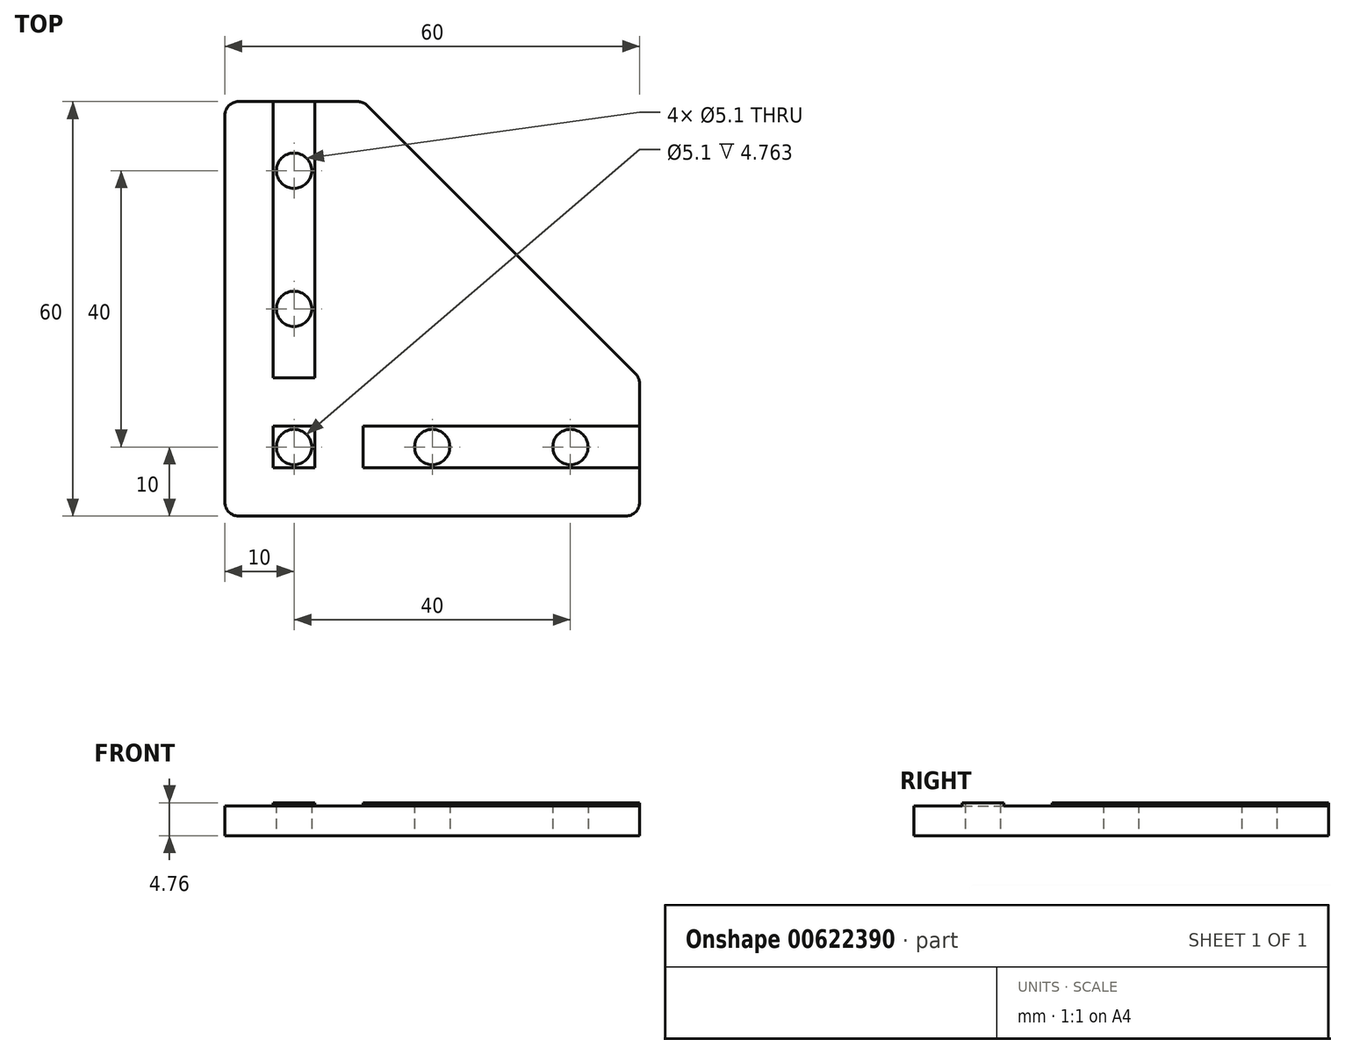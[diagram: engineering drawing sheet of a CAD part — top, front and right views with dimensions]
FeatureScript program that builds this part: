
annotation { "Feature Type Name" : "Feature", "Feature Type Description" : "" }
export const myFeature = defineFeature(function(context is Context, id is Id, definition is map)
    precondition{}
    {
        {
            assignVariable(context, id + "F0", {"name" : "TotalThick", "anyValue" : 4.76});
        }
        {
            assignVariable(context, id + "F1", {"name" : "Recess", "anyValue" : 0.5});
        }
        {
            var Q0;
            Q0=qCreatedBy(makeId("Top.planeOp"),FACE);
            var sketch = newSketch(context, id + "F2", { "sketchPlane" : qUnion([Q0])});
            skLineSegment(sketch, "E0", {"start": v(-10, 50) * mm, "end": v(-10, -10) * mm});
            skLineSegment(sketch, "E1", {"start": v(-10, -10) * mm, "end": v(50, -10) * mm});
            skLineSegment(sketch, "E2", {"start": v(50, -10) * mm, "end": v(50, 10) * mm});
            skLineSegment(sketch, "E3", {"start": v(50, 10) * mm, "end": v(10, 50) * mm});
            skLineSegment(sketch, "E4", {"start": v(10, 50) * mm, "end": v(-10, 50) * mm});
            skCircle(sketch, "E5", {"center": v(0, 0) * mm, "radius": 2.55 * mm});
            skCircle(sketch, "E6", {"center": v(0, 20) * mm, "radius": 2.55 * mm});
            skCircle(sketch, "E7", {"center": v(0, 40) * mm, "radius": 2.55 * mm});
            skCircle(sketch, "E8", {"center": v(20, 0) * mm, "radius": 2.55 * mm});
            skCircle(sketch, "E9", {"center": v(40, 0) * mm, "radius": 2.55 * mm});
            skLineSegment(sketch, "E10", {"start": v(-3.02, 50) * mm, "end": v(-3.03, -10) * mm});
            skLineSegment(sketch, "E11.MirrorCS", {"start": v(3.03, 50) * mm, "end": v(3.02, -10) * mm});
            skLineSegment(sketch, "E12", {"start": v(-10, 3.03) * mm, "end": v(50, 3.02) * mm});
            skLineSegment(sketch, "E13.MirrorCS", {"start": v(-10, -3.03) * mm, "end": v(50, -3.02) * mm});
            skLineSegment(sketch, "E14", {"start": v(10, 50) * mm, "end": v(10, -10) * mm});
            skLineSegment(sketch, "E15", {"start": v(50, 10) * mm, "end": v(-10, 10) * mm});
            skSolve(sketch);
        }
        {
            var Q0;
            Q0=qSketchRegion(id+"F2",true);
            var Q1;
            {var subQ0=sQuery(id+"F2.wireOp",EDGE,"E15");var subQ1=sQuery(id+"F2.wireOp",EDGE,"E11.MirrorCS");var subQ2=makeQuery(id+"F2.imprint","INTERSECT",VERTEX,{"derivedFrom":[subQ1,subQ0]});Q1=makeQuery(id+"F2.imprint","IMPRINT",FACE,{"disambiguationData":[TD([[makeQuery(id+"F2.imprint","IMPRINT",EDGE,{"disambiguationData":[TD([[subQ2,-1.0]])],"derivedFrom":subQ1}),1.0]])]});}
            var Q2;
            {var subQ0=sQuery(id+"F2.wireOp",EDGE,"E12");var subQ1=sQuery(id+"F2.wireOp",EDGE,"E11.MirrorCS");var subQ2=makeQuery(id+"F2.imprint","INTERSECT",VERTEX,{"derivedFrom":[subQ1,subQ0]});Q2=makeQuery(id+"F2.imprint","IMPRINT",FACE,{"disambiguationData":[TD([[makeQuery(id+"F2.imprint","IMPRINT",EDGE,{"disambiguationData":[TD([[subQ2,-1.0]])],"derivedFrom":subQ1}),1.0]])]});}
            var Q3;
            Q3=makeQuery(id+"F2.imprint","IMPRINT",FACE,{"disambiguationData":[TD([[makeQuery(id+"F2.imprint","IMPRINT",EDGE,{"derivedFrom":sQuery(id+"F2.wireOp",EDGE,"E5")}),-1.0]])]});
            var Q4;
            {var subQ0=sQuery(id+"F2.wireOp",EDGE,"E15");var subQ1=sQuery(id+"F2.wireOp",EDGE,"E10");var subQ2=makeQuery(id+"F2.imprint","INTERSECT",VERTEX,{"derivedFrom":[subQ1,subQ0]});Q4=makeQuery(id+"F2.imprint","IMPRINT",FACE,{"disambiguationData":[TD([[makeQuery(id+"F2.imprint","IMPRINT",EDGE,{"disambiguationData":[TD([[subQ2,-1.0]])],"derivedFrom":subQ1}),1.0]])]});}
            extrude(context, id + "F3", {"entities" : qUnion([Q0, Q1, Q2, Q3, Q4]), "depth" : (getVariable(context, 'TotalThick') - getVariable(context, 'Recess')) * mm, "offsetDistance" : 25 * mm});
        }
        {
            var Q0;
            Q0=makeQuery(id+"F2.imprint","IMPRINT",FACE,{"disambiguationData":[TD([[makeQuery(id+"F2.imprint","IMPRINT",EDGE,{"derivedFrom":sQuery(id+"F2.wireOp",EDGE,"E5")}),-1.0]])]});
            var Q1;
            Q1=makeQuery(id+"F2.imprint","IMPRINT",FACE,{"disambiguationData":[TD([[makeQuery(id+"F2.imprint","IMPRINT",EDGE,{"derivedFrom":sQuery(id+"F2.wireOp",EDGE,"E8")}),-1.0]])]});
            var Q2;
            Q2=makeQuery(id+"F2.imprint","IMPRINT",FACE,{"disambiguationData":[TD([[makeQuery(id+"F2.imprint","IMPRINT",EDGE,{"derivedFrom":sQuery(id+"F2.wireOp",EDGE,"E6")}),-1.0]])]});
            extrude(context, id + "F4", {"entities" : qUnion([Q0, Q1, Q2]), "operationType" : NewBodyOperationType.ADD, "depth" : (getVariable(context, 'TotalThick')) * mm, "offsetDistance" : 25 * mm});
        }
        {
            var Q0;
            Q0=makeQuery(id+"F3.opExtrude","SWEPT_EDGE",EDGE,{"disambiguationData":[OSD([sQuery(id+"F2.wireOp",EDGE,"E2"),sQuery(id+"F2.wireOp",EDGE,"E3"),sQuery(id+"F2.wireOp",EDGE,"E15")])]});
            var Q1;
            Q1=makeQuery(id+"F3.opExtrude","SWEPT_EDGE",EDGE,{"disambiguationData":[OSD([sQuery(id+"F2.wireOp",EDGE,"E1"),sQuery(id+"F2.wireOp",EDGE,"E2")])]});
            var Q2;
            Q2=makeQuery(id+"F3.opExtrude","SWEPT_EDGE",EDGE,{"disambiguationData":[OSD([sQuery(id+"F2.wireOp",EDGE,"E0"),sQuery(id+"F2.wireOp",EDGE,"E1")])]});
            var Q3;
            Q3=makeQuery(id+"F3.opExtrude","SWEPT_EDGE",EDGE,{"disambiguationData":[OSD([sQuery(id+"F2.wireOp",EDGE,"E0"),sQuery(id+"F2.wireOp",EDGE,"E4")])]});
            var Q4;
            Q4=makeQuery(id+"F3.opExtrude","SWEPT_EDGE",EDGE,{"disambiguationData":[OSD([sQuery(id+"F2.wireOp",EDGE,"E3"),sQuery(id+"F2.wireOp",EDGE,"E4"),sQuery(id+"F2.wireOp",EDGE,"E14")])]});
            fillet(context, id + "F5", {"entities" : qUnion([Q0, Q1, Q2, Q3, Q4]), "radius" : 2 * mm, "tangentPropagation" : true, "allowEdgeOverflow" : false});
        }
    });
